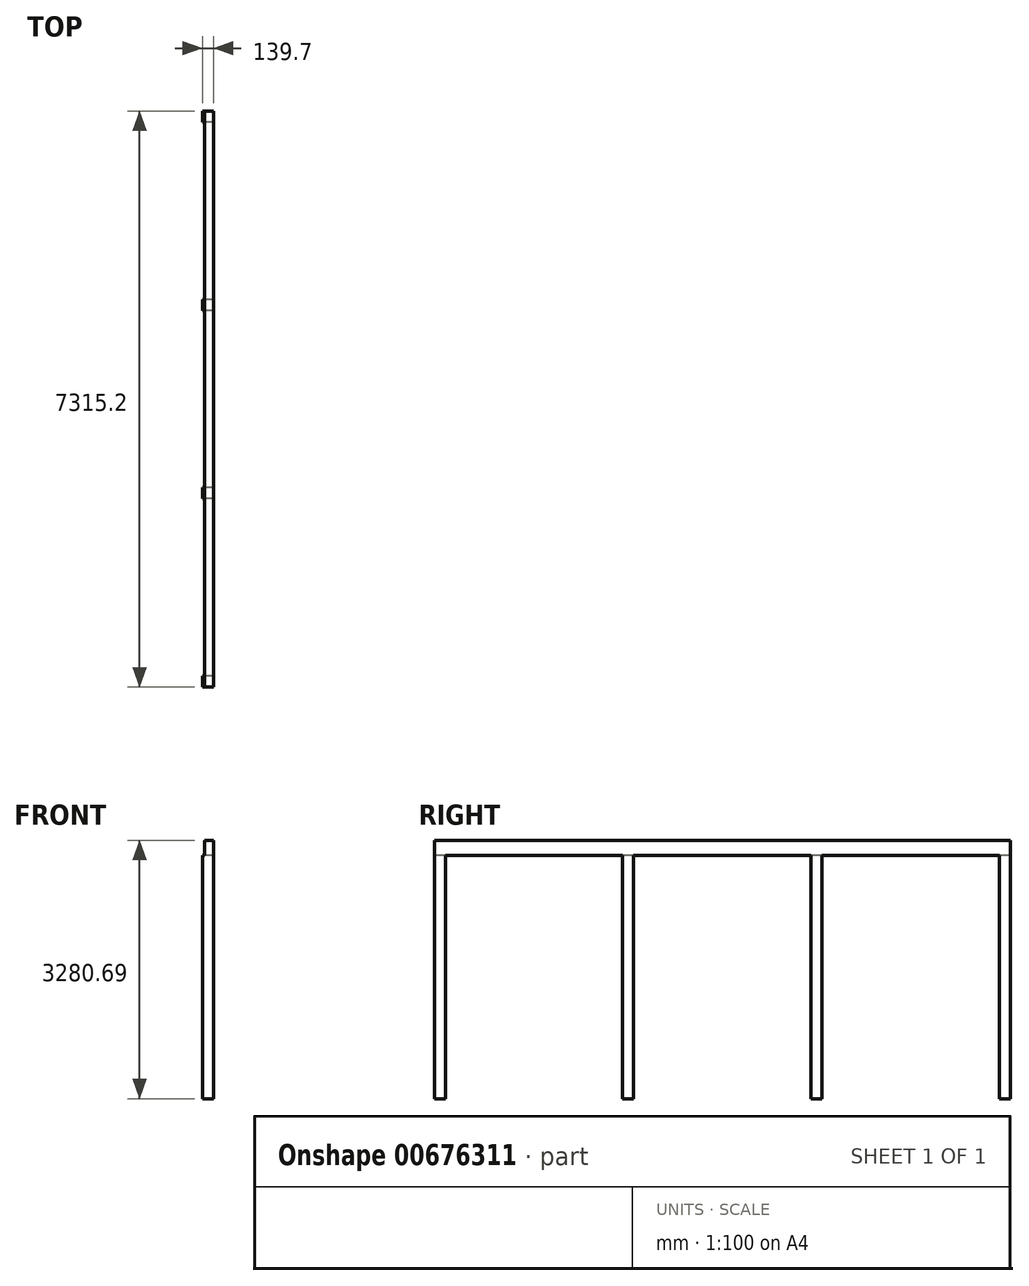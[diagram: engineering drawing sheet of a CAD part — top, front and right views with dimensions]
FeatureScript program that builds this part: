
annotation { "Feature Type Name" : "Feature", "Feature Type Description" : "" }
export const myFeature = defineFeature(function(context is Context, id is Id, definition is map)
    precondition{}
    {
        {
            var Q0;
            Q0=qCreatedBy(makeId("Top.planeOp"),FACE);
            var sketch = newSketch(context, id + "F0", { "sketchPlane" : qUnion([Q0])});
            skLineSegment(sketch, "E0.bottom", {"start": v(57.15, 3657.6) * mm, "end": v(-57.15, 3657.6) * mm});
            skLineSegment(sketch, "E0.top", {"start": v(57.15, -3657.6) * mm, "end": v(-57.15, -3657.6) * mm});
            skLineSegment(sketch, "E0.left", {"start": v(57.15, 3657.6) * mm, "end": v(57.15, -3657.6) * mm});
            skLineSegment(sketch, "E0.right", {"start": v(-57.15, 3657.6) * mm, "end": v(-57.15, -3657.6) * mm});
            skPoint(sketch, "E0.middle", {"position": v(0, 0) * mm});
            skSolve(sketch);
        }
        {
            var Q0;
            Q0 = qSketchRegion(id + "F0", true);
            extrude(context, id + "F1", {"entities" : qUnion([Q0]), "oppositeDirection" : true, "depth" : 190.5 * mm, "offsetDistance" : 25.4 * mm});
        }
        {
            var Q0;
            Q0=makeQuery(id+"F1.opExtrude","CAP_FACE",FACE,{"disambiguationData":[OSD([sQuery(id+"F0.wireOp",EDGE,"E0.bottom"),sQuery(id+"F0.wireOp",EDGE,"E0.top"),sQuery(id+"F0.wireOp",EDGE,"E0.left"),sQuery(id+"F0.wireOp",EDGE,"E0.right")])],"isStart":false});
            var sketch = newSketch(context, id + "F2", { "sketchPlane" : qUnion([Q0])});
            skLineSegment(sketch, "E1.bottom", {"start": v(57.15, 3657.6) * mm, "end": v(-82.55, 3657.6) * mm});
            skLineSegment(sketch, "E1.top", {"start": v(57.15, 3517.9) * mm, "end": v(-82.55, 3517.9) * mm});
            skLineSegment(sketch, "E1.left", {"start": v(57.15, 3657.6) * mm, "end": v(57.15, 3517.9) * mm});
            skLineSegment(sketch, "E1.right", {"start": v(-82.55, 3657.6) * mm, "end": v(-82.55, 3517.9) * mm});
            skLineSegment(sketch, "E2.bottom", {"start": v(57.15, 1265.77) * mm, "end": v(-82.55, 1265.77) * mm});
            skLineSegment(sketch, "E2.top", {"start": v(57.15, 1126.07) * mm, "end": v(-82.55, 1126.07) * mm});
            skLineSegment(sketch, "E2.left", {"start": v(57.15, 1265.77) * mm, "end": v(57.15, 1126.07) * mm});
            skLineSegment(sketch, "E2.right", {"start": v(-82.55, 1265.77) * mm, "end": v(-82.55, 1126.07) * mm});
            skLineSegment(sketch, "E3.bottom", {"start": v(57.15, -1126.07) * mm, "end": v(-82.55, -1126.07) * mm});
            skLineSegment(sketch, "E3.top", {"start": v(57.15, -1265.77) * mm, "end": v(-82.55, -1265.77) * mm});
            skLineSegment(sketch, "E3.left", {"start": v(57.15, -1126.07) * mm, "end": v(57.15, -1265.77) * mm});
            skLineSegment(sketch, "E3.right", {"start": v(-82.55, -1126.07) * mm, "end": v(-82.55, -1265.77) * mm});
            skLineSegment(sketch, "E4.bottom", {"start": v(57.15, -3657.6) * mm, "end": v(-82.55, -3657.6) * mm});
            skLineSegment(sketch, "E4.top", {"start": v(57.15, -3517.9) * mm, "end": v(-82.55, -3517.9) * mm});
            skLineSegment(sketch, "E4.left", {"start": v(57.15, -3657.6) * mm, "end": v(57.15, -3517.9) * mm});
            skLineSegment(sketch, "E4.right", {"start": v(-82.55, -3657.6) * mm, "end": v(-82.55, -3517.9) * mm});
            skLineSegment(sketch, "E5", {"start": v(-82.55, 3517.9) * mm, "end": v(-82.55, 1265.77) * mm, "construction": true});
            skLineSegment(sketch, "E6", {"start": v(-82.55, 1126.07) * mm, "end": v(-82.55, -1126.07) * mm, "construction": true});
            skLineSegment(sketch, "E7", {"start": v(-82.55, -1265.77) * mm, "end": v(-82.55, -3517.9) * mm, "construction": true});
            skSolve(sketch);
        }
        {
            var Q0;
            Q0 = qSketchRegion(id + "F2", true);
            extrude(context, id + "F3", {"entities" : qUnion([Q0]), "operationType" : NewBodyOperationType.ADD, "depth" : 3090.2 * mm, "offsetDistance" : 25.4 * mm});
        }
    });
